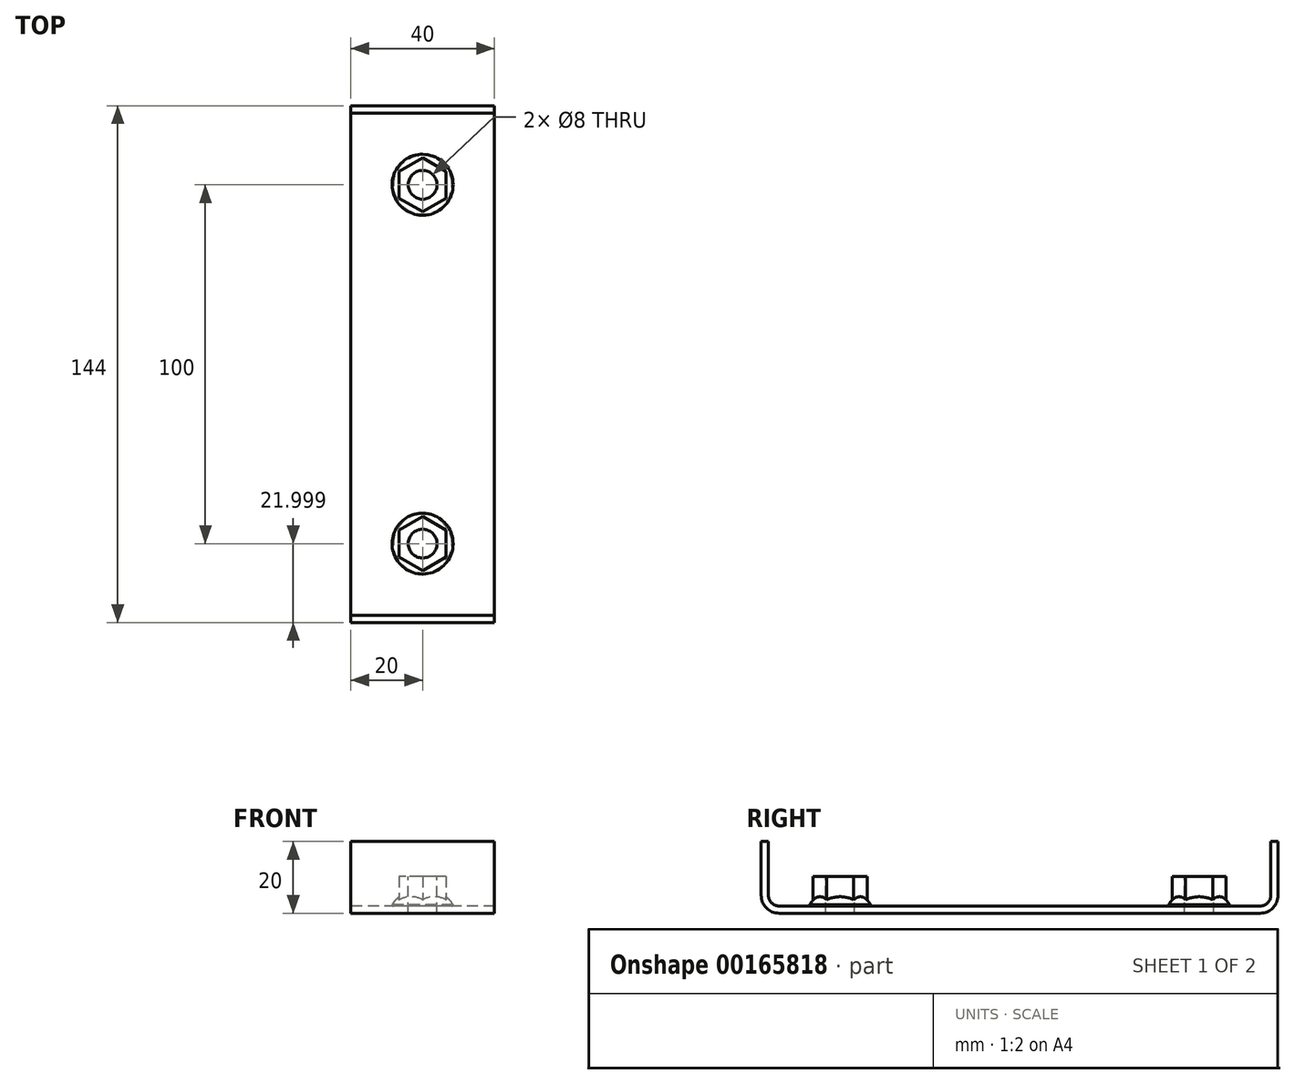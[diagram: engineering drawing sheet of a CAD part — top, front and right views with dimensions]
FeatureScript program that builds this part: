
annotation { "Feature Type Name" : "Feature", "Feature Type Description" : "" }
export const myFeature = defineFeature(function(context is Context, id is Id, definition is map)
    precondition{}
    {
        {
            var Q0;
            Q0=qCreatedBy(makeId("Top.planeOp"),FACE);
            var sketch = newSketch(context, id + "F0", { "sketchPlane" : qUnion([Q0])});
            skCircle(sketch, "E0", {"center": v(0, 1.19) * mm, "radius": 8.5 * mm});
            skSolve(sketch);
        }
        {
            var Q0;
            Q0=makeQuery(id+"F0.imprint","IMPRINT",FACE,{"disambiguationData":[TD([[makeQuery(id+"F0.imprint","IMPRINT",EDGE,{"derivedFrom":sQuery(id+"F0.wireOp",EDGE,"E0")}),1.0]])]});
            extrude(context, id + "F1", {"entities" : qUnion([Q0]), "depth" : .25 * mm});
        }
        {
            var Q0;
            Q0=makeQuery(id+"F1.opExtrude","CAP_FACE",FACE,{"disambiguationData":[OSD([sQuery(id+"F0.wireOp",EDGE,"E0")])],"isStart":false});
            extrude(context, id + "F2", {"entities" : qUnion([Q0]), "operationType" : NewBodyOperationType.ADD, "depth" : 4 * mm});
        }
        {
            var Q0;
            Q0=makeQuery(id+"F1.opExtrude","CAP_EDGE",EDGE,{"disambiguationData":[OSD([sQuery(id+"F0.wireOp",EDGE,"E0")])],"isStart":true});
            fillet(context, id + "F3", {"entities" : qUnion([Q0]), "radius" : .35 * mm, "tangentPropagation" : true, "allowEdgeOverflow" : false});
        }
        {
            var Q0;
            Q0=makeQuery(id+"F2.opExtrude","CAP_EDGE",EDGE,{"disambiguationData":[OSD([sQuery(id+"F0.wireOp",EDGE,"E0")])],"isStart":false});
            fillet(context, id + "F4", {"entities" : qUnion([Q0]), "radius" : 8 * mm, "allowEdgeOverflow" : false});
        }
        {
            var Q0;
            Q0=makeQuery(id+"F2.opExtrude","CAP_FACE",FACE,{"disambiguationData":[OSD([sQuery(id+"F0.wireOp",EDGE,"E0")])],"isStart":false});
            cPlane(context, id + "F5", {"entities" : qUnion([Q0]), "cplaneType" : CPlaneType.OFFSET, "offset" : 2 * mm, "oppositeDirection" : true, "width" : 150 * mm, "height" : 150 * mm});
        }
        {
            var Q0;
            Q0=qCreatedBy(id+"F5.planeOp",FACE);
            var sketch = newSketch(context, id + "F6", { "sketchPlane" : qUnion([Q0])});
            skCircle(sketch, "E1.0", {"center": v(0, 1.19) * mm, "radius": 1.63 * mm, "construction": true});
            skCircle(sketch, "E2.cCircle", {"center": v(0, 1.19) * mm, "radius": 6.5 * mm, "construction": true});
            skLineSegment(sketch, "E2.0", {"start": v(-6.5, -2.56) * mm, "end": v(-6.5, 4.94) * mm});
            skLineSegment(sketch, "E2.1", {"start": v(-6.5, 4.94) * mm, "end": v(0, 8.7) * mm});
            skLineSegment(sketch, "E2.2", {"start": v(0, 8.7) * mm, "end": v(6.5, 4.94) * mm});
            skLineSegment(sketch, "E2.3", {"start": v(6.5, 4.94) * mm, "end": v(6.5, -2.56) * mm});
            skLineSegment(sketch, "E2.4", {"start": v(6.5, -2.56) * mm, "end": v(0, -6.32) * mm});
            skLineSegment(sketch, "E2.5", {"start": v(0, -6.32) * mm, "end": v(-6.5, -2.56) * mm});
            skPoint(sketch, "E2.0.midPoint", {"position": v(-6.5, 1.19) * mm});
            skSolve(sketch);
        }
        {
            var Q0;
            Q0 = qSketchRegion(id + "F6", true);
            var Q1;
            Q1=makeQuery(id+"F1.opExtrude","CAP_FACE",FACE,{"disambiguationData":[OSD([sQuery(id+"F0.wireOp",EDGE,"E0")])],"isStart":true});
            extrude(context, id + "F7", {"entities" : qUnion([Q0]), "operationType" : NewBodyOperationType.ADD, "depth" : 6 * mm, "hasSecondDirection" : true, "secondDirectionBound" : SecondDirectionBoundingType.UP_TO_SURFACE, "secondDirectionOppositeDirection" : true, "secondDirectionBoundEntityFace" : qUnion([Q1]), "secondDirectionDepth" : 25 * mm});
        }
        {
            var Q0;
            Q0=makeQuery(id+"F7.opExtrude","CAP_FACE",FACE,{"disambiguationData":[OSD([sQuery(id+"F6.wireOp",EDGE,"E2.0"),sQuery(id+"F6.wireOp",EDGE,"E2.1"),sQuery(id+"F6.wireOp",EDGE,"E2.2"),sQuery(id+"F6.wireOp",EDGE,"E2.3"),sQuery(id+"F6.wireOp",EDGE,"E2.4"),sQuery(id+"F6.wireOp",EDGE,"E2.5")])],"isStart":false});
            var sketch = newSketch(context, id + "F8", { "sketchPlane" : qUnion([Q0])});
            skCircle(sketch, "E3", {"center": v(0, 1.19) * mm, "radius": 4 * mm});
            skLineSegment(sketch, "E4", {"start": v(0, 1.19) * mm, "end": v(3.25, 6.82) * mm, "construction": true});
            skLineSegment(sketch, "E5", {"start": v(3.25, -4.44) * mm, "end": v(0, 1.19) * mm, "construction": true});
            skSolve(sketch);
        }
        {
            var Q0;
            Q0=makeQuery(id+"F8.imprint","IMPRINT",FACE,{"disambiguationData":[TD([[makeQuery(id+"F8.imprint","IMPRINT",EDGE,{"derivedFrom":sQuery(id+"F8.wireOp",EDGE,"E3")}),1.0]])]});
            extrude(context, id + "F9", {"entities" : qUnion([Q0]), "operationType" : NewBodyOperationType.REMOVE, "endBound" : BoundingType.THROUGH_ALL, "oppositeDirection" : true, "depth" : 25 * mm});
        }
        {
            var Q0;
            Q0=qCreatedBy(makeId("Right.planeOp"),FACE);
            var sketch = newSketch(context, id + "F10", { "sketchPlane" : qUnion([Q0])});
            skLineSegment(sketch, "E6", {"start": v(21.19, 18) * mm, "end": v(21.19, 0) * mm});
            skLineSegment(sketch, "E7", {"start": v(21.19, 0) * mm, "end": v(-118.81, 0) * mm});
            skLineSegment(sketch, "E8", {"start": v(-118.81, 0) * mm, "end": v(-118.81, 18) * mm});
            skLineSegment(sketch, "E9", {"start": v(-118.81, 18) * mm, "end": v(-120.81, 18) * mm});
            skLineSegment(sketch, "E10", {"start": v(-120.81, 18) * mm, "end": v(-120.81, -2) * mm});
            skLineSegment(sketch, "E11", {"start": v(-120.81, -2) * mm, "end": v(23.19, -2) * mm});
            skLineSegment(sketch, "E12", {"start": v(23.19, -2) * mm, "end": v(23.19, 18) * mm});
            skLineSegment(sketch, "E13", {"start": v(23.19, 18) * mm, "end": v(21.19, 18) * mm});
            skSolve(sketch);
        }
        {
            var Q0;
            Q0=makeQuery(id+"F10.imprint","IMPRINT",FACE,{"disambiguationData":[TD([[makeQuery(id+"F10.imprint","IMPRINT",EDGE,{"derivedFrom":sQuery(id+"F10.wireOp",EDGE,"E6")}),1.0]])]});
            extrude(context, id + "F11", {"entities" : qUnion([Q0]), "operationType" : NewBodyOperationType.ADD, "depth" : 20 * mm, "hasSecondDirection" : true, "secondDirectionOppositeDirection" : true, "secondDirectionDepth" : 20 * mm});
        }
        {
            var Q0;
            Q0=makeQuery(id+"F11.opExtrude","CAP_EDGE",EDGE,{"disambiguationData":[OSD([sQuery(id+"F10.wireOp",EDGE,"E7")])],"isStart":true});
            cPoint(context, id + "F12", {"entities" : qUnion([Q0]), "parameter" : 0.5});
        }
        {
            var Q0;
            Q0=makeQuery(id+"F11.opExtrude","CAP_EDGE",EDGE,{"disambiguationData":[OSD([sQuery(id+"F10.wireOp",EDGE,"E7")])],"isStart":false});
            cPoint(context, id + "F13", {"entities" : qUnion([Q0]), "parameter" : 0.5});
        }
        {
            var Q0;
            Q0=makeQuery(id+"F11.opExtrude","CAP_EDGE",EDGE,{"disambiguationData":[OSD([sQuery(id+"F10.wireOp",EDGE,"E11")])],"isStart":true});
            cPoint(context, id + "F14", {"entities" : qUnion([Q0]), "parameter" : 0.5});
        }
        {
            var Q0;
            Q0 = qCreatedBy(id + "F12" ,VERTEX);
            var Q1;
            Q1 = qCreatedBy(id + "F13" ,VERTEX);
            var Q2;
            Q2 = qCreatedBy(id + "F14" ,VERTEX);
            cPlane(context, id + "F15", {"entities" : qUnion([Q0, Q1, Q2]), "cplaneType" : CPlaneType.THREE_POINT, "offset" : 25 * mm, "width" : 150 * mm, "height" : 150 * mm});
        }
        {
            var Q0;
            Q0=makeQuery(id+"F1.opExtrude","SWEPT_BODY",BODY,{"disambiguationData":[OSD([sQuery(id+"F0.wireOp",EDGE,"E0")])]});
            var Q1;
            Q1=qCreatedBy(id+"F15.planeOp",FACE);
            mirror(context, id + "F16", {"operationType" : NewBodyOperationType.ADD, "entities" : qUnion([Q0]), "mirrorPlane" : qUnion([Q1])});
        }
        {
            var Q0;
            Q0=makeQuery(id+"F11.opExtrude","SWEPT_EDGE",EDGE,{"disambiguationData":[OSD([sQuery(id+"F10.wireOp",EDGE,"E11"),sQuery(id+"F10.wireOp",EDGE,"E12")])]});
            var Q1;
            Q1=makeQuery(id+"F11.opExtrude","SWEPT_EDGE",EDGE,{"disambiguationData":[OSD([sQuery(id+"F10.wireOp",EDGE,"E10"),sQuery(id+"F10.wireOp",EDGE,"E11")])]});
            fillet(context, id + "F17", {"entities" : qUnion([Q0, Q1]), "radius" : 5 * mm, "tangentPropagation" : true, "allowEdgeOverflow" : false});
        }
        {
            var Q0;
            Q0=makeQuery(id+"F11.opExtrude","SWEPT_EDGE",EDGE,{"disambiguationData":[OSD([sQuery(id+"F10.wireOp",EDGE,"E6"),sQuery(id+"F10.wireOp",EDGE,"E7")])]});
            var Q1;
            Q1=makeQuery(id+"F11.opExtrude","SWEPT_EDGE",EDGE,{"disambiguationData":[OSD([sQuery(id+"F10.wireOp",EDGE,"E7"),sQuery(id+"F10.wireOp",EDGE,"E8")])]});
            fillet(context, id + "F18", {"entities" : qUnion([Q0, Q1]), "radius" : 3 * mm, "tangentPropagation" : true, "allowEdgeOverflow" : false});
        }
        {
            var Q0;
            Q0=makeQuery(id+"F11.boolean.opBoolean","SPLIT",FACE,{"disambiguationData":[TD([makeQuery(id+"F9.boolean.opBoolean","COPY",FACE,{"derivedFrom":makeQuery(id+"F9.opExtrude","SWEPT_FACE",FACE,{"disambiguationData":[OSD([sQuery(id+"F8.wireOp",EDGE,"E3")])]})})])],"derivedFrom":makeQuery(id+"F11.opExtrude","SWEPT_FACE",FACE,{"disambiguationData":[OSD([sQuery(id+"F10.wireOp",EDGE,"E7")])]})});
            var Q1;
            {var subQ6=sQuery(id+"F10.wireOp",EDGE,"E7");Q1=makeQuery(id+"F16.boolean.opBoolean","SPLIT",FACE,{"disambiguationData":[TD([makeQuery(id+"F16.opPattern","COPY",FACE,{"derivedFrom":makeQuery(id+"F9.boolean.opBoolean","COPY",FACE,{"derivedFrom":makeQuery(id+"F9.opExtrude","SWEPT_FACE",FACE,{"disambiguationData":[OSD([sQuery(id+"F8.wireOp",EDGE,"E3")])]})}),"instanceName":"1"})])],"derivedFrom":makeQuery(id+"F11.boolean.opBoolean","SPLIT",FACE,{"disambiguationData":[TD([makeQuery(id+"F3.opFillet","BLEND_FACE",FACE,{"disambiguationData":[OSD([sQuery(id+"F0.wireOp",EDGE,"E0")])]})])],"derivedFrom":makeQuery(id+"F11.opExtrude","SWEPT_FACE",FACE,{"disambiguationData":[OSD([subQ6])]})})});}
            extrude(context, id + "F19", {"entities" : qUnion([Q0, Q1]), "operationType" : NewBodyOperationType.REMOVE, "oppositeDirection" : true, "depth" : 25 * mm});
        }
    });
